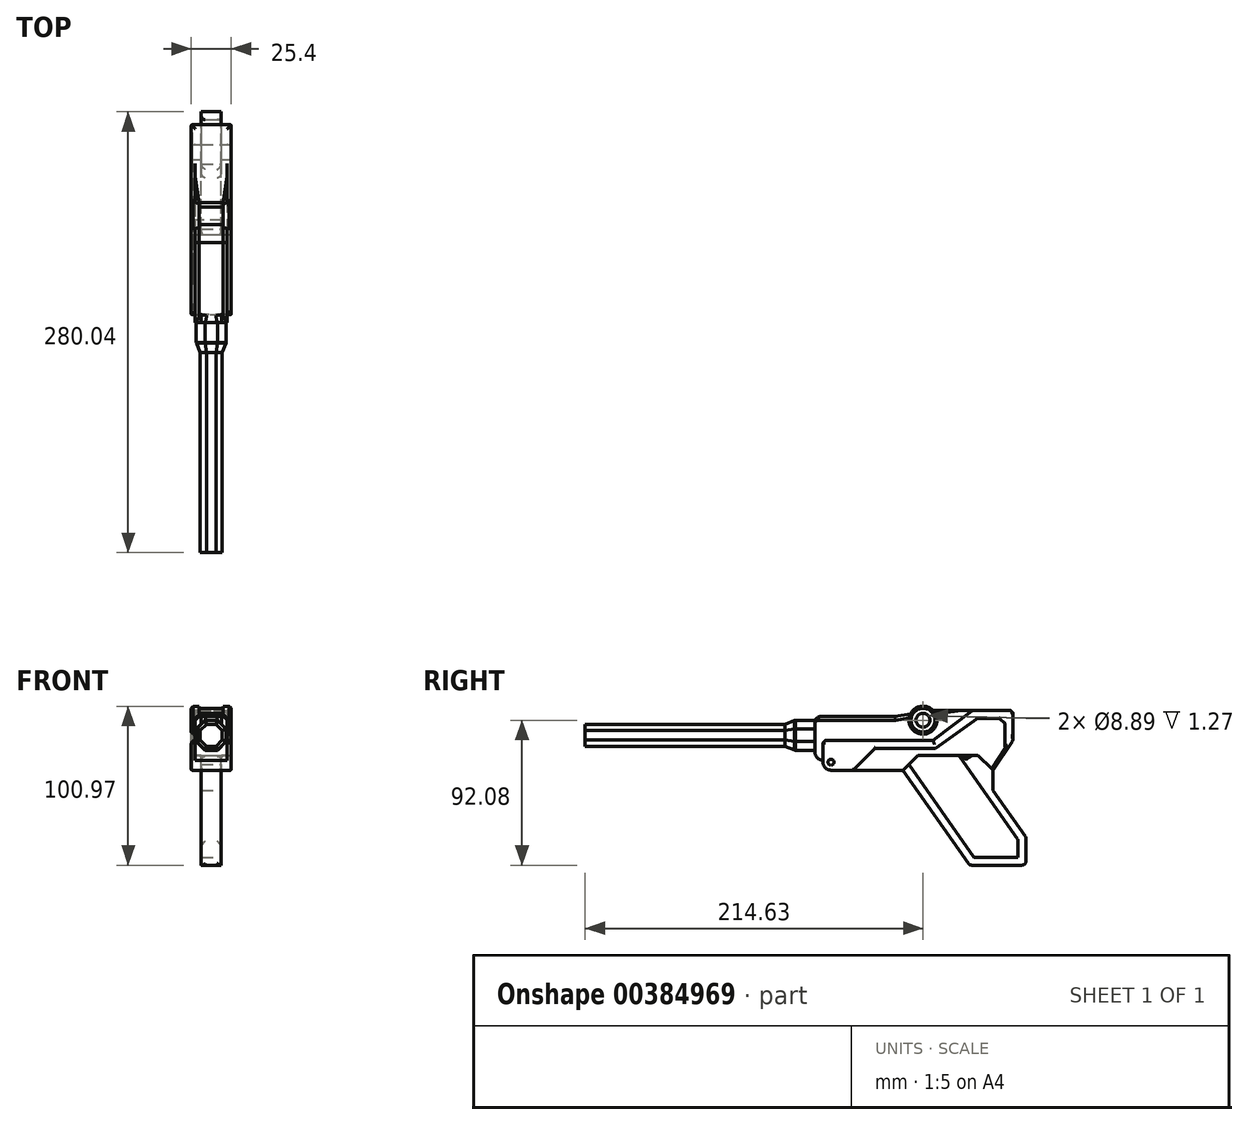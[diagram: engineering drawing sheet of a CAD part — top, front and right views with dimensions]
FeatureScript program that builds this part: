
annotation { "Feature Type Name" : "Feature", "Feature Type Description" : "" }
export const myFeature = defineFeature(function(context is Context, id is Id, definition is map)
    precondition{}
    {
        {
            var Q0;
            Q0=qCreatedBy(makeId("Front.planeOp"),FACE);
            var sketch = newSketch(context, id + "F0", { "sketchPlane" : qUnion([Q0])});
            skLineSegment(sketch, "E0", {"start": v(-76.2, 44.45) * mm, "end": v(-76.2, 25.4) * mm});
            skLineSegment(sketch, "E1", {"start": v(-76.2, 25.4) * mm, "end": v(-63.5, 6.35) * mm});
            skLineSegment(sketch, "E2", {"start": v(-6.35, 6.35) * mm, "end": v(44.45, 6.35) * mm});
            skLineSegment(sketch, "E3", {"start": v(-50.8, 44.45) * mm, "end": v(-25.4, 25.4) * mm});
            skLineSegment(sketch, "E4", {"start": v(-25.4, 25.4) * mm, "end": v(44.45, 25.4) * mm});
            skLineSegment(sketch, "E5", {"start": v(-76.2, 44.45) * mm, "end": v(-50.8, 44.45) * mm});
            skLineSegment(sketch, "E6", {"start": v(44.45, 25.4) * mm, "end": v(44.45, 6.35) * mm});
            skLineSegment(sketch, "E7", {"start": v(-63.5, 6.35) * mm, "end": v(-53.98, 15.88) * mm});
            skLineSegment(sketch, "E8", {"start": v(-53.98, 15.88) * mm, "end": v(-15.88, 15.88) * mm});
            skLineSegment(sketch, "E9", {"start": v(-15.88, 15.88) * mm, "end": v(-6.35, 6.35) * mm});
            skSolve(sketch);
        }
        {
            var Q0;
            Q0=makeQuery(id+"F0.imprint","IMPRINT",FACE,{"disambiguationData":[TD([[makeQuery(id+"F0.imprint","IMPRINT",EDGE,{"derivedFrom":sQuery(id+"F0.wireOp",EDGE,"E0")}),1.0]])]});
            extrude(context, id + "F1", {"entities" : qUnion([Q0]), "endBound" : BoundingType.SYMMETRIC, "depth" : 25.4 * mm});
        }
        {
            var Q0;
            Q0=makeQuery(id+"F1.opExtrude","SWEPT_FACE",FACE,{"disambiguationData":[OSD([sQuery(id+"F0.wireOp",EDGE,"E5")])]});
            var Q1;
            Q1=makeQuery(id+"F1.opExtrude","SWEPT_EDGE",EDGE,{"disambiguationData":[OSD([sQuery(id+"F0.wireOp",EDGE,"E4"),sQuery(id+"F0.wireOp",EDGE,"E6")])]});
            var Q2;
            Q2=makeQuery(id+"F1.opExtrude","CAP_EDGE",EDGE,{"disambiguationData":[OSD([sQuery(id+"F0.wireOp",EDGE,"E4")])],"isStart":false});
            var Q3;
            Q3=makeQuery(id+"F1.opExtrude","CAP_EDGE",EDGE,{"disambiguationData":[OSD([sQuery(id+"F0.wireOp",EDGE,"E4")])],"isStart":true});
            var Q4;
            Q4=makeQuery(id+"F1.opExtrude","CAP_EDGE",EDGE,{"disambiguationData":[OSD([sQuery(id+"F0.wireOp",EDGE,"E3")])],"isStart":false});
            var Q5;
            Q5=makeQuery(id+"F1.opExtrude","CAP_EDGE",EDGE,{"disambiguationData":[OSD([sQuery(id+"F0.wireOp",EDGE,"E3")])],"isStart":true});
            var Q6;
            Q6=makeQuery(id+"F1.opExtrude","SWEPT_EDGE",EDGE,{"disambiguationData":[OSD([sQuery(id+"F0.wireOp",EDGE,"E0"),sQuery(id+"F0.wireOp",EDGE,"E1")])]});
            var Q7;
            Q7=makeQuery(id+"F1.opExtrude","CAP_EDGE",EDGE,{"disambiguationData":[OSD([sQuery(id+"F0.wireOp",EDGE,"E1")])],"isStart":false});
            var Q8;
            Q8=makeQuery(id+"F1.opExtrude","CAP_EDGE",EDGE,{"disambiguationData":[OSD([sQuery(id+"F0.wireOp",EDGE,"E1")])],"isStart":true});
            fillet(context, id + "F2", {"entities" : qUnion([Q0, Q1, Q2, Q3, Q4, Q5, Q6, Q7, Q8]), "radius" : 2.54 * mm, "tangentPropagation" : true, "allowEdgeOverflow" : false});
        }
        {
            var Q0;
            Q0=qCreatedBy(makeId("Front.planeOp"),FACE);
            var sketch = newSketch(context, id + "F3", { "sketchPlane" : qUnion([Q0])});
            skLineSegment(sketch, "E10", {"start": v(-1.27, 40.64) * mm, "end": v(49.53, 40.64) * mm});
            skLineSegment(sketch, "E11", {"start": v(49.53, 40.64) * mm, "end": v(49.53, 12.7) * mm});
            skLineSegment(sketch, "E12", {"start": v(-52.07, 44.45) * mm, "end": v(-26.67, 44.45) * mm});
            skLineSegment(sketch, "E13", {"start": v(-26.67, 44.45) * mm, "end": v(-1.27, 40.64) * mm});
            skLineSegment(sketch, "E14", {"start": v(-52.07, 44.45) * mm, "end": v(-52.07, 28.57) * mm});
            skLineSegment(sketch, "E15", {"start": v(-52.07, 28.57) * mm, "end": v(0, 12.7) * mm});
            skLineSegment(sketch, "E16", {"start": v(0, 12.7) * mm, "end": v(49.53, 12.7) * mm});
            skSolve(sketch);
        }
        {
            var Q0;
            Q0=makeQuery(id+"F3.imprint","IMPRINT",FACE,{"disambiguationData":[TD([[makeQuery(id+"F3.imprint","IMPRINT",EDGE,{"derivedFrom":sQuery(id+"F3.wireOp",EDGE,"E10")}),-1.0]])]});
            extrude(context, id + "F4", {"entities" : qUnion([Q0]), "operationType" : NewBodyOperationType.ADD, "endBound" : BoundingType.SYMMETRIC, "depth" : 20.32 * mm});
        }
        {
            var Q0;
            Q0=makeQuery(id+"F4.opExtrude","CAP_EDGE",EDGE,{"disambiguationData":[OSD([sQuery(id+"F3.wireOp",EDGE,"E10")])],"isStart":false});
            var Q1;
            Q1=makeQuery(id+"F4.opExtrude","CAP_EDGE",EDGE,{"disambiguationData":[OSD([sQuery(id+"F3.wireOp",EDGE,"E10")])],"isStart":true});
            var Q2;
            Q2=makeQuery(id+"F4.opExtrude","CAP_EDGE",EDGE,{"disambiguationData":[OSD([sQuery(id+"F3.wireOp",EDGE,"E13")])],"isStart":false});
            var Q3;
            Q3=makeQuery(id+"F4.opExtrude","CAP_EDGE",EDGE,{"disambiguationData":[OSD([sQuery(id+"F3.wireOp",EDGE,"E13")])],"isStart":true});
            chamfer(context, id + "F5", {"entities" : qUnion([Q0, Q1, Q2, Q3]), "width" : 2.54 * mm, "tangentPropagation" : true});
        }
        {
            var Q0;
            Q0=makeQuery(id+"F4.opExtrude","CAP_FACE",FACE,{"disambiguationData":[OSD([sQuery(id+"F3.wireOp",EDGE,"E10"),sQuery(id+"F3.wireOp",EDGE,"E11"),sQuery(id+"F3.wireOp",EDGE,"FEaoXIQV-EktY-PLqT-aak4-A0hKiz9UVHVJ"),sQuery(id+"F3.wireOp",EDGE,"tK53UXBf-cSsi-bV3R-Xlyo-zfIDGGMdSWBN"),sQuery(id+"F3.wireOp",EDGE,"E12"),sQuery(id+"F3.wireOp",EDGE,"E13")])],"isStart":false});
            var sketch = newSketch(context, id + "F6", { "sketchPlane" : qUnion([Q0])});
            skCircle(sketch, "E17", {"center": v(-19.05, 38.1) * mm, "radius": 8.9 * mm});
            skCircle(sketch, "E18", {"center": v(-19.05, 38.1) * mm, "radius": 4.45 * mm});
            skSolve(sketch);
        }
        {
            var Q0;
            {var subQ0=sQuery(id+"F6.wireOp",EDGE,"E17");var subQ1=sQuery(id+"F3.wireOp",EDGE,"E13");var subQ2=makeQuery(id+"F5.opChamfer","BLEND_EDGE",EDGE,{"blendedFrom":[makeQuery(id+"F4.opExtrude","CAP_EDGE",EDGE,{"disambiguationData":[OSD([subQ1])],"isStart":false}),makeQuery(id+"F4.opExtrude","CAP_FACE",FACE,{"disambiguationData":[OSD([sQuery(id+"F3.wireOp",EDGE,"E10"),sQuery(id+"F3.wireOp",EDGE,"E11"),sQuery(id+"F3.wireOp",EDGE,"FEaoXIQV-EktY-PLqT-aak4-A0hKiz9UVHVJ"),sQuery(id+"F3.wireOp",EDGE,"tK53UXBf-cSsi-bV3R-Xlyo-zfIDGGMdSWBN"),sQuery(id+"F3.wireOp",EDGE,"E12"),subQ1])],"isStart":false})],"blendedInto":[makeQuery(id+"F4.opExtrude","CAP_FACE",FACE,{"disambiguationData":[OSD([sQuery(id+"F3.wireOp",EDGE,"E10"),sQuery(id+"F3.wireOp",EDGE,"E11"),sQuery(id+"F3.wireOp",EDGE,"FEaoXIQV-EktY-PLqT-aak4-A0hKiz9UVHVJ"),sQuery(id+"F3.wireOp",EDGE,"tK53UXBf-cSsi-bV3R-Xlyo-zfIDGGMdSWBN"),sQuery(id+"F3.wireOp",EDGE,"E12"),subQ1])],"isStart":false})]});var subQ3=makeQuery(id+"F6.imprint","INTERSECT",VERTEX,{"disambiguationData":[OD(0.0)],"derivedFrom":[subQ2,subQ0]});Q0=makeQuery(id+"F6.imprint","IMPRINT",FACE,{"disambiguationData":[TD([[makeQuery(id+"F6.imprint","IMPRINT",EDGE,{"disambiguationData":[TD([[subQ3,-1.0]])],"derivedFrom":subQ0}),1.0]])]});}
            var Q1;
            {var subQ0=sQuery(id+"F6.wireOp",EDGE,"E17");var subQ1=sQuery(id+"F3.wireOp",EDGE,"E13");var subQ2=makeQuery(id+"F5.opChamfer","BLEND_EDGE",EDGE,{"blendedFrom":[makeQuery(id+"F4.opExtrude","CAP_EDGE",EDGE,{"disambiguationData":[OSD([subQ1])],"isStart":false}),makeQuery(id+"F4.opExtrude","CAP_FACE",FACE,{"disambiguationData":[OSD([sQuery(id+"F3.wireOp",EDGE,"E10"),sQuery(id+"F3.wireOp",EDGE,"E11"),sQuery(id+"F3.wireOp",EDGE,"FEaoXIQV-EktY-PLqT-aak4-A0hKiz9UVHVJ"),sQuery(id+"F3.wireOp",EDGE,"tK53UXBf-cSsi-bV3R-Xlyo-zfIDGGMdSWBN"),sQuery(id+"F3.wireOp",EDGE,"E12"),subQ1])],"isStart":false})],"blendedInto":[makeQuery(id+"F4.opExtrude","CAP_FACE",FACE,{"disambiguationData":[OSD([sQuery(id+"F3.wireOp",EDGE,"E10"),sQuery(id+"F3.wireOp",EDGE,"E11"),sQuery(id+"F3.wireOp",EDGE,"FEaoXIQV-EktY-PLqT-aak4-A0hKiz9UVHVJ"),sQuery(id+"F3.wireOp",EDGE,"tK53UXBf-cSsi-bV3R-Xlyo-zfIDGGMdSWBN"),sQuery(id+"F3.wireOp",EDGE,"E12"),subQ1])],"isStart":false})]});var subQ3=makeQuery(id+"F6.imprint","INTERSECT",VERTEX,{"disambiguationData":[OD(0.0)],"derivedFrom":[subQ2,subQ0]});Q1=makeQuery(id+"F6.imprint","IMPRINT",FACE,{"disambiguationData":[TD([[makeQuery(id+"F6.imprint","IMPRINT",EDGE,{"disambiguationData":[TD([[subQ3,1.0]])],"derivedFrom":subQ0}),1.0]])]});}
            extrude(context, id + "F7", {"entities" : qUnion([Q0, Q1]), "operationType" : NewBodyOperationType.ADD, "endBound" : BoundingType.SYMMETRIC, "depth" : 5.08 * mm});
        }
        {
            var Q0;
            Q0=makeQuery(id+"F4.opExtrude","CAP_FACE",FACE,{"disambiguationData":[OSD([sQuery(id+"F3.wireOp",EDGE,"E10"),sQuery(id+"F3.wireOp",EDGE,"E11"),sQuery(id+"F3.wireOp",EDGE,"FEaoXIQV-EktY-PLqT-aak4-A0hKiz9UVHVJ"),sQuery(id+"F3.wireOp",EDGE,"tK53UXBf-cSsi-bV3R-Xlyo-zfIDGGMdSWBN"),sQuery(id+"F3.wireOp",EDGE,"E12"),sQuery(id+"F3.wireOp",EDGE,"E13")])],"isStart":true});
            var sketch = newSketch(context, id + "F8", { "sketchPlane" : qUnion([Q0])});
            skCircle(sketch, "E19", {"center": v(19.05, 38.1) * mm, "radius": 8.9 * mm});
            skCircle(sketch, "E20", {"center": v(19.05, 38.1) * mm, "radius": 4.45 * mm});
            skSolve(sketch);
        }
        {
            var Q0;
            Q0 = qSketchRegion(id + "F8", true);
            extrude(context, id + "F9", {"entities" : qUnion([Q0]), "operationType" : NewBodyOperationType.ADD, "endBound" : BoundingType.SYMMETRIC, "depth" : 5.08 * mm});
        }
        {
            var Q0;
            Q0=qCreatedBy(makeId("Front.planeOp"),FACE);
            var sketch = newSketch(context, id + "F10", { "sketchPlane" : qUnion([Q0])});
            skCircle(sketch, "E21", {"center": v(-19.05, 38.1) * mm, "radius": 7.62 * mm});
            skSolve(sketch);
        }
        {
            var Q0;
            Q0 = qSketchRegion(id + "F10", true);
            extrude(context, id + "F11", {"entities" : qUnion([Q0]), "operationType" : NewBodyOperationType.ADD, "endBound" : BoundingType.SYMMETRIC, "depth" : 22.86 * mm});
        }
        {
            var Q0;
            Q0=makeQuery(id+"F7.opExtrude","CAP_EDGE",EDGE,{"disambiguationData":[OSD([sQuery(id+"F6.wireOp",EDGE,"E17")])],"isStart":false});
            chamfer(context, id + "F12", {"entities" : qUnion([Q0]), "width" : 1.27 * mm, "tangentPropagation" : true});
        }
        {
            var Q0;
            Q0=makeQuery(id+"F9.opExtrude","CAP_EDGE",EDGE,{"disambiguationData":[OSD([sQuery(id+"F8.wireOp",EDGE,"E19")])],"isStart":false});
            chamfer(context, id + "F13", {"entities" : qUnion([Q0]), "width" : 1.27 * mm, "tangentPropagation" : true});
        }
        {
            var Q0;
            Q0=makeQuery(id+"F1.opExtrude","CAP_FACE",FACE,{"disambiguationData":[OSD([sQuery(id+"F0.wireOp",EDGE,"E0"),sQuery(id+"F0.wireOp",EDGE,"E1"),sQuery(id+"F0.wireOp",EDGE,"E2"),sQuery(id+"F0.wireOp",EDGE,"E3"),sQuery(id+"F0.wireOp",EDGE,"E4"),sQuery(id+"F0.wireOp",EDGE,"E5"),sQuery(id+"F0.wireOp",EDGE,"E6"),sQuery(id+"F0.wireOp",EDGE,"E7"),sQuery(id+"F0.wireOp",EDGE,"E8"),sQuery(id+"F0.wireOp",EDGE,"E9")])],"isStart":true});
            var sketch = newSketch(context, id + "F14", { "sketchPlane" : qUnion([Q0])});
            skArc(sketch, "E22", {"start": v(-44.45, 11.43) * mm, "mid": v(-42.96, 7.84) * mm, "end": v(-39.37, 6.35) * mm});
            skLineSegment(sketch, "E23", {"start": v(-44.45, 11.43) * mm, "end": v(-44.45, 6.35) * mm});
            skLineSegment(sketch, "E24", {"start": v(-44.45, 6.35) * mm, "end": v(-39.37, 6.35) * mm});
            skSolve(sketch);
        }
        {
            var Q0;
            {var subQ0=sQuery(id+"F14.wireOp",EDGE,"E22");Q0=makeQuery(id+"F14.imprint","IMPRINT",FACE,{"disambiguationData":[TD([[makeQuery(id+"F14.imprint","IMPRINT",EDGE,{"derivedFrom":subQ0}),-1.0]])]});}
            extrude(context, id + "F15", {"entities" : qUnion([Q0]), "operationType" : NewBodyOperationType.REMOVE, "oppositeDirection" : true, "depth" : 25.4 * mm});
        }
        {
            var Q0;
            Q0=makeQuery(id+"F4.opExtrude","SWEPT_FACE",FACE,{"disambiguationData":[OSD([sQuery(id+"F3.wireOp",EDGE,"E11")])]});
            var sketch = newSketch(context, id + "F16", { "sketchPlane" : qUnion([Q0])});
            skCircle(sketch, "E25.cCircle", {"center": v(0, 28.58) * mm, "radius": 9.53 * mm, "construction": true});
            skLineSegment(sketch, "E25.0", {"start": v(3.95, 38.1) * mm, "end": v(9.53, 32.52) * mm});
            skLineSegment(sketch, "E25.1", {"start": v(9.52, 32.52) * mm, "end": v(9.52, 24.63) * mm});
            skLineSegment(sketch, "E25.2", {"start": v(9.52, 24.63) * mm, "end": v(3.95, 19.05) * mm});
            skLineSegment(sketch, "E25.3", {"start": v(3.95, 19.05) * mm, "end": v(-3.95, 19.05) * mm});
            skLineSegment(sketch, "E25.4", {"start": v(-3.95, 19.05) * mm, "end": v(-9.52, 24.63) * mm});
            skLineSegment(sketch, "E25.5", {"start": v(-9.52, 24.63) * mm, "end": v(-9.52, 32.52) * mm});
            skLineSegment(sketch, "E25.6", {"start": v(-9.52, 32.52) * mm, "end": v(-3.95, 38.1) * mm});
            skLineSegment(sketch, "E25.7", {"start": v(-3.95, 38.1) * mm, "end": v(3.95, 38.1) * mm});
            skPoint(sketch, "E25.0.midPoint", {"position": v(6.74, 35.31) * mm});
            skSolve(sketch);
        }
        {
            var Q0;
            Q0=qCreatedBy(makeId("Front.planeOp"),FACE);
            var sketch = newSketch(context, id + "F17", { "sketchPlane" : qUnion([Q0])});
            skLineSegment(sketch, "E26", {"start": v(49.53, 38.1) * mm, "end": v(62.23, 38.1) * mm});
            skLineSegment(sketch, "E27", {"start": v(62.23, 38.1) * mm, "end": v(68.58, 35.56) * mm});
            skLineSegment(sketch, "E28", {"start": v(68.58, 35.56) * mm, "end": v(195.58, 35.56) * mm});
            skLineSegment(sketch, "E29", {"start": v(195.58, 35.56) * mm, "end": v(195.58, 28.58) * mm});
            skLineSegment(sketch, "E30", {"start": v(49.53, 38.1) * mm, "end": v(49.53, 28.58) * mm});
            skLineSegment(sketch, "E31", {"start": v(49.53, 28.58) * mm, "end": v(195.58, 28.58) * mm});
            skSolve(sketch);
        }
        {
            var Q0;
            Q0=makeQuery(id+"F17.imprint","IMPRINT",FACE,{"disambiguationData":[TD([[makeQuery(id+"F17.imprint","IMPRINT",EDGE,{"derivedFrom":sQuery(id+"F17.wireOp",EDGE,"E26")}),-1.0]])]});
            var Q1;
            Q1 = qConstructionFilter(qBodyType(qCreatedBy(id + "F16" ,EDGE), BodyType.WIRE), ConstructionObject.NO);
            sweep(context, id + "F18", {"operationType" : NewBodyOperationType.ADD, "profiles" : qUnion([Q0]), "path" : qUnion([Q1])});
        }
        {
            var Q0;
            Q0=makeQuery(id+"F18.opSweep","SWEPT_EDGE",EDGE,{"disambiguationData":[OSD([sQuery(id+"F16.wireOp",EDGE,"E25.7"),sQuery(id+"F17.wireOp",EDGE,"E26"),sQuery(id+"F17.wireOp",EDGE,"E27")])]});
            var Q1;
            Q1=makeQuery(id+"F18.opSweep","SWEPT_EDGE",EDGE,{"disambiguationData":[OSD([sQuery(id+"F16.wireOp",EDGE,"E25.6"),sQuery(id+"F17.wireOp",EDGE,"E26"),sQuery(id+"F17.wireOp",EDGE,"E27")])]});
            var Q2;
            Q2=makeQuery(id+"F18.opSweep","SWEPT_EDGE",EDGE,{"disambiguationData":[OSD([sQuery(id+"F16.wireOp",EDGE,"E25.5"),sQuery(id+"F17.wireOp",EDGE,"E26"),sQuery(id+"F17.wireOp",EDGE,"E27")])]});
            var Q3;
            Q3=makeQuery(id+"F18.opSweep","SWEPT_EDGE",EDGE,{"disambiguationData":[OSD([sQuery(id+"F16.wireOp",EDGE,"E25.0"),sQuery(id+"F17.wireOp",EDGE,"E26"),sQuery(id+"F17.wireOp",EDGE,"E27")])]});
            var Q4;
            Q4=makeQuery(id+"F18.opSweep","SWEPT_EDGE",EDGE,{"disambiguationData":[OSD([sQuery(id+"F16.wireOp",EDGE,"E25.1"),sQuery(id+"F17.wireOp",EDGE,"E26"),sQuery(id+"F17.wireOp",EDGE,"E27")])]});
            var Q5;
            Q5=makeQuery(id+"F18.opSweep","SWEPT_EDGE",EDGE,{"disambiguationData":[OSD([sQuery(id+"F16.wireOp",EDGE,"E25.2"),sQuery(id+"F17.wireOp",EDGE,"E26"),sQuery(id+"F17.wireOp",EDGE,"E27")])]});
            var Q6;
            Q6=makeQuery(id+"F18.opSweep","SWEPT_EDGE",EDGE,{"disambiguationData":[OSD([sQuery(id+"F16.wireOp",EDGE,"E25.3"),sQuery(id+"F17.wireOp",EDGE,"E26"),sQuery(id+"F17.wireOp",EDGE,"E27")])]});
            var Q7;
            Q7=makeQuery(id+"F18.opSweep","SWEPT_EDGE",EDGE,{"disambiguationData":[OSD([sQuery(id+"F16.wireOp",EDGE,"E25.4"),sQuery(id+"F17.wireOp",EDGE,"E26"),sQuery(id+"F17.wireOp",EDGE,"E27")])]});
            chamfer(context, id + "F19", {"entities" : qUnion([Q0, Q1, Q2, Q3, Q4, Q5, Q6, Q7]), "width" : 1.27 * mm, "tangentPropagation" : true});
        }
        {
            var Q0;
            Q0=makeQuery(id+"F4.opExtrude","SWEPT_EDGE",EDGE,{"disambiguationData":[OSD([sQuery(id+"F3.wireOp",EDGE,"E11"),sQuery(id+"F3.wireOp",EDGE,"FEaoXIQV-EktY-PLqT-aak4-A0hKiz9UVHVJ")])]});
            fillet(context, id + "F20", {"entities" : qUnion([Q0]), "radius" : 5.08 * mm, "tangentPropagation" : true, "allowEdgeOverflow" : false});
        }
        {
            var Q0;
            Q0=makeQuery(id+"F1.opExtrude","CAP_FACE",FACE,{"disambiguationData":[OSD([sQuery(id+"F0.wireOp",EDGE,"E0"),sQuery(id+"F0.wireOp",EDGE,"E1"),sQuery(id+"F0.wireOp",EDGE,"E2"),sQuery(id+"F0.wireOp",EDGE,"E3"),sQuery(id+"F0.wireOp",EDGE,"E4"),sQuery(id+"F0.wireOp",EDGE,"E5"),sQuery(id+"F0.wireOp",EDGE,"E6"),sQuery(id+"F0.wireOp",EDGE,"E7"),sQuery(id+"F0.wireOp",EDGE,"E8"),sQuery(id+"F0.wireOp",EDGE,"E9")])],"isStart":true});
            var sketch = newSketch(context, id + "F21", { "sketchPlane" : qUnion([Q0])});
            skCircle(sketch, "E32", {"center": v(-39.37, 11.43) * mm, "radius": 1.9 * mm});
            skSolve(sketch);
        }
        {
            var Q0;
            Q0=makeQuery(id+"F1.opExtrude","CAP_FACE",FACE,{"disambiguationData":[OSD([sQuery(id+"F0.wireOp",EDGE,"E0"),sQuery(id+"F0.wireOp",EDGE,"E1"),sQuery(id+"F0.wireOp",EDGE,"E2"),sQuery(id+"F0.wireOp",EDGE,"E3"),sQuery(id+"F0.wireOp",EDGE,"E4"),sQuery(id+"F0.wireOp",EDGE,"E5"),sQuery(id+"F0.wireOp",EDGE,"E6"),sQuery(id+"F0.wireOp",EDGE,"E7"),sQuery(id+"F0.wireOp",EDGE,"E8"),sQuery(id+"F0.wireOp",EDGE,"E9")])],"isStart":false});
            var sketch = newSketch(context, id + "F22", { "sketchPlane" : qUnion([Q0])});
            skCircle(sketch, "E33", {"center": v(39.37, 11.43) * mm, "radius": 1.9 * mm});
            skSolve(sketch);
        }
        {
            var Q0;
            Q0 = qSketchRegion(id + "F22", true);
            extrude(context, id + "F23", {"entities" : qUnion([Q0]), "operationType" : NewBodyOperationType.REMOVE, "oppositeDirection" : true, "depth" : 0.5 * mm});
        }
        {
            var Q0;
            Q0 = qSketchRegion(id + "F21", true);
            extrude(context, id + "F24", {"entities" : qUnion([Q0]), "operationType" : NewBodyOperationType.REMOVE, "oppositeDirection" : true, "depth" : 0.5 * mm});
        }
        {
            var Q0;
            Q0=makeQuery(id+"F1.opExtrude","CAP_FACE",FACE,{"disambiguationData":[OSD([sQuery(id+"F0.wireOp",EDGE,"E0"),sQuery(id+"F0.wireOp",EDGE,"E1"),sQuery(id+"F0.wireOp",EDGE,"E2"),sQuery(id+"F0.wireOp",EDGE,"E3"),sQuery(id+"F0.wireOp",EDGE,"E4"),sQuery(id+"F0.wireOp",EDGE,"E5"),sQuery(id+"F0.wireOp",EDGE,"E6"),sQuery(id+"F0.wireOp",EDGE,"E7"),sQuery(id+"F0.wireOp",EDGE,"E8"),sQuery(id+"F0.wireOp",EDGE,"E9")])],"isStart":false});
            var sketch = newSketch(context, id + "F25", { "sketchPlane" : qUnion([Q0])});
            skLineSegment(sketch, "E34", {"start": v(-71.12, 0) * mm, "end": v(-71.12, 35.94) * mm});
            skPoint(sketch, "E34.endSnap0", {"position": v(-76.2, 35.94) * mm});
            skLineSegment(sketch, "E35", {"start": v(-71.12, 35.94) * mm, "end": v(-67.7, 39.37) * mm});
            skLineSegment(sketch, "E36", {"start": v(-67.7, 39.37) * mm, "end": v(-53.55, 39.37) * mm});
            skLineSegment(sketch, "E37", {"start": v(-53.55, 39.37) * mm, "end": v(-27.1, 20.32) * mm});
            skLineSegment(sketch, "E38", {"start": v(-27.1, 20.32) * mm, "end": v(11.43, 20.32) * mm});
            skLineSegment(sketch, "E39", {"start": v(11.43, 20.32) * mm, "end": v(25.4, 6.35) * mm});
            skLineSegment(sketch, "E40", {"start": v(25.4, 6.35) * mm, "end": v(25.4, 0) * mm});
            skLineSegment(sketch, "E41", {"start": v(25.4, 0) * mm, "end": v(-71.12, 0) * mm});
            skSolve(sketch);
        }
        {
            var Q0;
            Q0=makeQuery(id+"F1.opExtrude","CAP_FACE",FACE,{"disambiguationData":[OSD([sQuery(id+"F0.wireOp",EDGE,"E0"),sQuery(id+"F0.wireOp",EDGE,"E1"),sQuery(id+"F0.wireOp",EDGE,"E2"),sQuery(id+"F0.wireOp",EDGE,"E3"),sQuery(id+"F0.wireOp",EDGE,"E4"),sQuery(id+"F0.wireOp",EDGE,"E5"),sQuery(id+"F0.wireOp",EDGE,"E6"),sQuery(id+"F0.wireOp",EDGE,"E7"),sQuery(id+"F0.wireOp",EDGE,"E8"),sQuery(id+"F0.wireOp",EDGE,"E9")])],"isStart":true});
            var sketch = newSketch(context, id + "F26", { "sketchPlane" : qUnion([Q0])});
            skLineSegment(sketch, "E42", {"start": v(71.12, 0) * mm, "end": v(71.12, 35.94) * mm});
            skLineSegment(sketch, "E43", {"start": v(71.12, 35.94) * mm, "end": v(67.7, 39.37) * mm});
            skLineSegment(sketch, "E44", {"start": v(67.7, 39.37) * mm, "end": v(53.55, 39.37) * mm});
            skLineSegment(sketch, "E45", {"start": v(53.55, 39.37) * mm, "end": v(27.1, 20.32) * mm});
            skLineSegment(sketch, "E46", {"start": v(27.1, 20.32) * mm, "end": v(-11.43, 20.32) * mm});
            skLineSegment(sketch, "E47", {"start": v(-11.43, 20.32) * mm, "end": v(-25.4, 6.35) * mm});
            skLineSegment(sketch, "E48", {"start": v(-25.4, 6.35) * mm, "end": v(-25.4, 0) * mm});
            skLineSegment(sketch, "E49", {"start": v(-25.4, 0) * mm, "end": v(71.12, 0) * mm});
            skSolve(sketch);
        }
        {
            var Q0;
            Q0 = qSketchRegion(id + "F25", true);
            extrude(context, id + "F27", {"entities" : qUnion([Q0]), "operationType" : NewBodyOperationType.REMOVE, "oppositeDirection" : true, "depth" : 0.5 * mm});
        }
        {
            var Q0;
            Q0 = qSketchRegion(id + "F26", true);
            extrude(context, id + "F28", {"entities" : qUnion([Q0]), "operationType" : NewBodyOperationType.REMOVE, "oppositeDirection" : true, "depth" : 0.5 * mm});
        }
        {
            var Q0;
            Q0=makeQuery(id+"F1.opExtrude","CAP_FACE",FACE,{"disambiguationData":[OSD([sQuery(id+"F0.wireOp",EDGE,"E0"),sQuery(id+"F0.wireOp",EDGE,"E1"),sQuery(id+"F0.wireOp",EDGE,"E2"),sQuery(id+"F0.wireOp",EDGE,"E3"),sQuery(id+"F0.wireOp",EDGE,"E4"),sQuery(id+"F0.wireOp",EDGE,"E5"),sQuery(id+"F0.wireOp",EDGE,"E6"),sQuery(id+"F0.wireOp",EDGE,"E7"),sQuery(id+"F0.wireOp",EDGE,"E8"),sQuery(id+"F0.wireOp",EDGE,"E9")])],"isStart":false});
            fillet(context, id + "F29", {"entities" : qUnion([Q0]), "radius" : 0.5 * mm, "tangentPropagation" : true, "allowEdgeOverflow" : false});
        }
        {
            var Q0;
            Q0=makeQuery(id+"F1.opExtrude","CAP_FACE",FACE,{"disambiguationData":[OSD([sQuery(id+"F0.wireOp",EDGE,"E0"),sQuery(id+"F0.wireOp",EDGE,"E1"),sQuery(id+"F0.wireOp",EDGE,"E2"),sQuery(id+"F0.wireOp",EDGE,"E3"),sQuery(id+"F0.wireOp",EDGE,"E4"),sQuery(id+"F0.wireOp",EDGE,"E5"),sQuery(id+"F0.wireOp",EDGE,"E6"),sQuery(id+"F0.wireOp",EDGE,"E7"),sQuery(id+"F0.wireOp",EDGE,"E8"),sQuery(id+"F0.wireOp",EDGE,"E9")])],"isStart":true});
            fillet(context, id + "F30", {"entities" : qUnion([Q0]), "radius" : 0.5 * mm, "tangentPropagation" : true, "allowEdgeOverflow" : false});
        }
        {
            var Q0;
            Q0=qCreatedBy(makeId("Front.planeOp"),FACE);
            var sketch = newSketch(context, id + "F31", { "sketchPlane" : qUnion([Q0])});
            skLineSegment(sketch, "E50", {"start": v(-6.35, 6.35) * mm, "end": v(-30.8, -28.58) * mm});
            skLineSegment(sketch, "E51", {"start": v(-48.6, -53.98) * mm, "end": v(-84.45, -53.98) * mm});
            skLineSegment(sketch, "E52", {"start": v(-84.45, -36.28) * mm, "end": v(-63.5, -6.35) * mm});
            skLineSegment(sketch, "E53", {"start": v(-63.5, -6.35) * mm, "end": v(-63.5, 6.35) * mm});
            skLineSegment(sketch, "E54", {"start": v(-84.45, -53.98) * mm, "end": v(-84.45, -36.28) * mm});
            skPoint(sketch, "E54.startSnap0", {"position": v(-84.45, -36.28) * mm});
            skLineSegment(sketch, "E55", {"start": v(-10, 10) * mm, "end": v(-51.23, -48.9) * mm});
            skLineSegment(sketch, "E56", {"start": v(-51.23, -48.9) * mm, "end": v(-79.38, -48.9) * mm});
            skLineSegment(sketch, "E57", {"start": v(-79.38, -48.9) * mm, "end": v(-79.38, -37.88) * mm});
            skLineSegment(sketch, "E58", {"start": v(-79.38, -37.88) * mm, "end": v(-41.74, 15.88) * mm});
            skLineSegment(sketch, "E59", {"start": v(-30.8, -28.57) * mm, "end": v(-48.6, -53.98) * mm});
            skLineSegment(sketch, "E60", {"start": v(-10, 10) * mm, "end": v(-6.35, 6.35) * mm});
            skLineSegment(sketch, "E61", {"start": v(-41.74, 15.88) * mm, "end": v(-63.5, 15.88) * mm});
            skLineSegment(sketch, "E62", {"start": v(-63.5, 15.88) * mm, "end": v(-63.5, 6.35) * mm});
            skSolve(sketch);
        }
        {
            var Q0;
            Q0 = qSketchRegion(id + "F31", true);
            extrude(context, id + "F32", {"entities" : qUnion([Q0]), "operationType" : NewBodyOperationType.ADD, "endBound" : BoundingType.SYMMETRIC, "depth" : 12.7 * mm});
        }
        {
            var Q0;
            Q0=makeQuery(id+"F32.opExtrude","SWEPT_FACE",FACE,{"disambiguationData":[OSD([sQuery(id+"F31.wireOp",EDGE,"E58")])]});
            var Q1;
            Q1=makeQuery(id+"F32.opExtrude","CAP_EDGE",EDGE,{"disambiguationData":[OSD([sQuery(id+"F31.wireOp",EDGE,"E50"),sQuery(id+"F31.wireOp",EDGE,"E59")])],"isStart":true});
            var Q2;
            Q2=makeQuery(id+"F32.opExtrude","CAP_EDGE",EDGE,{"disambiguationData":[OSD([sQuery(id+"F31.wireOp",EDGE,"E50"),sQuery(id+"F31.wireOp",EDGE,"E59")])],"isStart":false});
            var Q3;
            Q3=makeQuery(id+"F32.opExtrude","SWEPT_EDGE",EDGE,{"disambiguationData":[OSD([sQuery(id+"F31.wireOp",EDGE,"E51"),sQuery(id+"F31.wireOp",EDGE,"E59")])]});
            var Q4;
            Q4=makeQuery(id+"F32.opExtrude","SWEPT_EDGE",EDGE,{"disambiguationData":[OSD([sQuery(id+"F31.wireOp",EDGE,"E51"),sQuery(id+"F31.wireOp",EDGE,"E54")])]});
            var Q5;
            Q5=makeQuery(id+"F32.opExtrude","SWEPT_EDGE",EDGE,{"disambiguationData":[OSD([sQuery(id+"F31.wireOp",EDGE,"E52"),sQuery(id+"F31.wireOp",EDGE,"E54")])]});
            fillet(context, id + "F33", {"entities" : qUnion([Q0, Q1, Q2, Q3, Q4, Q5]), "radius" : 2.54 * mm, "tangentPropagation" : true, "allowEdgeOverflow" : false});
        }
        {
            var Q0;
            Q0=qCreatedBy(makeId("Front.planeOp"),FACE);
            var sketch = newSketch(context, id + "F34", { "sketchPlane" : qUnion([Q0])});
            skLineSegment(sketch, "E63", {"start": v(0, 0) * mm, "end": v(0, 76.2) * mm});
            skSolve(sketch);
        }
        {
            var Q0;
            Q0=makeQuery(id+"F1.opExtrude","SWEPT_BODY",BODY,{"disambiguationData":[OSD([sQuery(id+"F0.wireOp",EDGE,"E0"),sQuery(id+"F0.wireOp",EDGE,"E1"),sQuery(id+"F0.wireOp",EDGE,"E2"),sQuery(id+"F0.wireOp",EDGE,"E3"),sQuery(id+"F0.wireOp",EDGE,"E4"),sQuery(id+"F0.wireOp",EDGE,"E5"),sQuery(id+"F0.wireOp",EDGE,"E6"),sQuery(id+"F0.wireOp",EDGE,"E7"),sQuery(id+"F0.wireOp",EDGE,"E8"),sQuery(id+"F0.wireOp",EDGE,"E9")])]});
            var Q1;
            Q1=sQuery(id+"F34.wireOp",EDGE,"E63");
            transform(context, id + "F35", {"entities" : qUnion([Q0]), "transformType" : TransformType.ROTATION, "transformAxis" : qUnion([Q1]), "angle" : 90 * degree, "oppositeDirection" : true, "makeCopy" : false});
        }
    });
